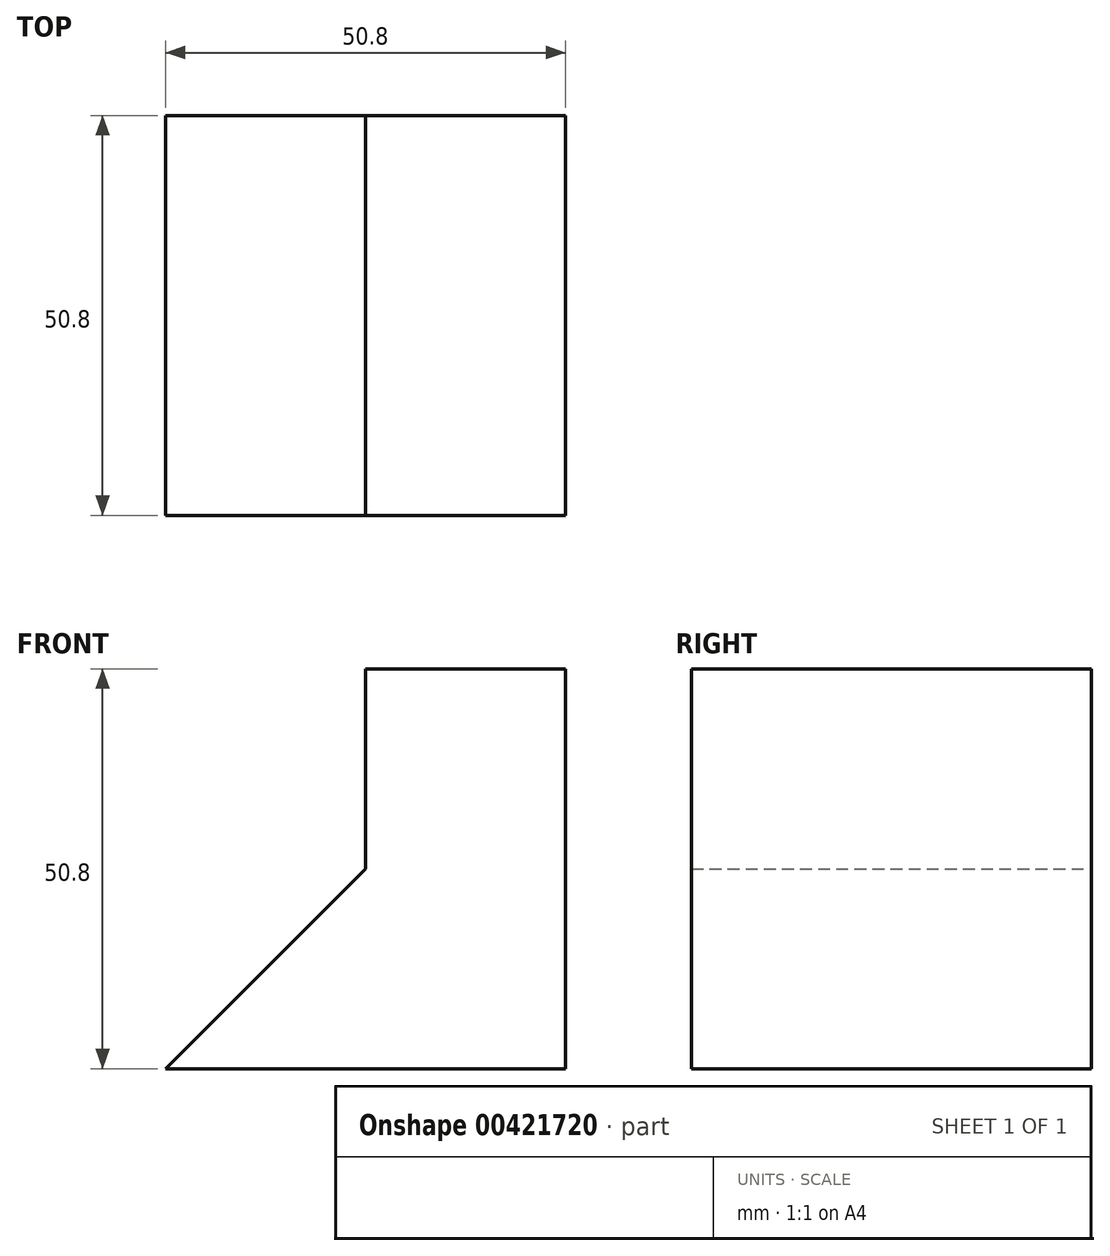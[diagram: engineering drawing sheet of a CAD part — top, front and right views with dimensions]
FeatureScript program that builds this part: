
annotation { "Feature Type Name" : "Feature", "Feature Type Description" : "" }
export const myFeature = defineFeature(function(context is Context, id is Id, definition is map)
    precondition{}
    {
        {
            var Q0;
            Q0=qCreatedBy(makeId("Front.planeOp"),FACE);
            var sketch = newSketch(context, id + "F0", { "sketchPlane" : qUnion([Q0])});
            skLineSegment(sketch, "E0", {"start": v(0, 0) * mm, "end": v(0, 50.8) * mm});
            skLineSegment(sketch, "E1", {"start": v(0, 50.8) * mm, "end": v(-25.4, 50.8) * mm});
            skLineSegment(sketch, "E2", {"start": v(-25.4, 50.8) * mm, "end": v(-25.4, 25.4) * mm});
            skLineSegment(sketch, "E3", {"start": v(-25.4, 25.4) * mm, "end": v(-50.8, 0) * mm});
            skLineSegment(sketch, "E4", {"start": v(-50.8, 0) * mm, "end": v(0, 0) * mm});
            skSolve(sketch);
        }
        {
            var Q0;
            Q0=makeQuery(id+"F0.imprint","IMPRINT",FACE,{"disambiguationData":[TD([[makeQuery(id+"F0.imprint","IMPRINT",EDGE,{"derivedFrom":sQuery(id+"F0.wireOp",EDGE,"E0")}),1.0]])]});
            extrude(context, id + "F1", {"entities" : qUnion([Q0]), "depth" : 50.8 * mm});
        }
    });
